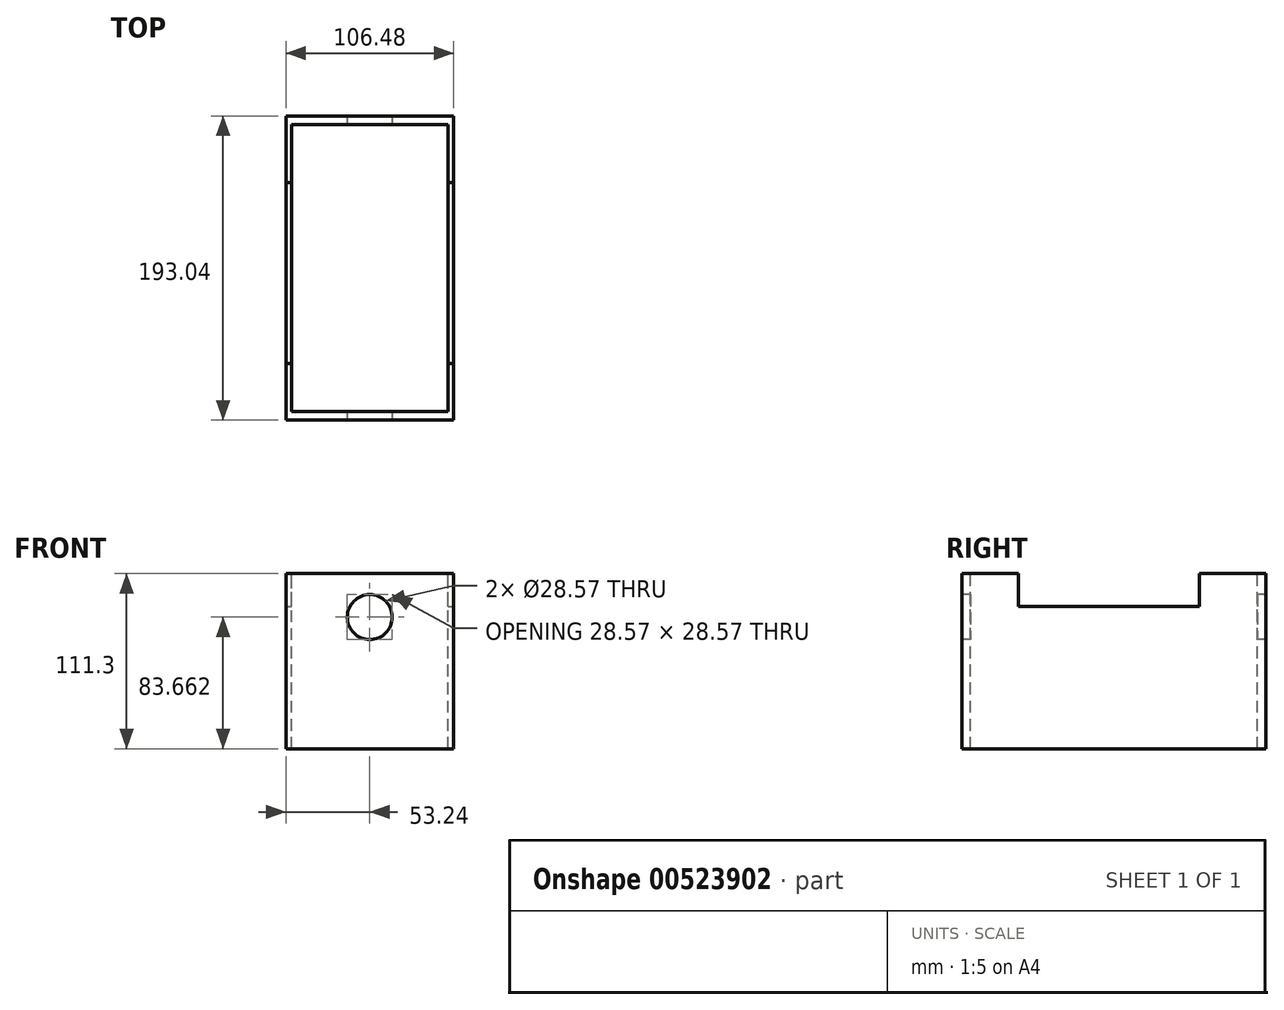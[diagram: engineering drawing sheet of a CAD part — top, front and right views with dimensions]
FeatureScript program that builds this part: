
annotation { "Feature Type Name" : "Feature", "Feature Type Description" : "" }
export const myFeature = defineFeature(function(context is Context, id is Id, definition is map)
    precondition{}
    {
        {
            var Q0;
            Q0=qCreatedBy(makeId("Front.planeOp"),FACE);
            var sketch = newSketch(context, id + "F0", { "sketchPlane" : qUnion([Q0])});
            skLineSegment(sketch, "E0.bottom", {"start": v(53.24, -55.65) * mm, "end": v(-53.24, -55.65) * mm});
            skLineSegment(sketch, "E0.top", {"start": v(53.24, 55.65) * mm, "end": v(-53.24, 55.65) * mm});
            skLineSegment(sketch, "E0.left", {"start": v(53.24, -55.65) * mm, "end": v(53.24, 55.65) * mm});
            skLineSegment(sketch, "E0.right", {"start": v(-53.24, -55.65) * mm, "end": v(-53.24, 55.65) * mm});
            skPoint(sketch, "E0.middle", {"position": v(0, 0) * mm});
            skSolve(sketch);
        }
        {
            var Q0;
            Q0=makeQuery(id+"F0.imprint","IMPRINT",FACE,{"disambiguationData":[TD([[makeQuery(id+"F0.imprint","IMPRINT",EDGE,{"derivedFrom":sQuery(id+"F0.wireOp",EDGE,"E0.bottom")}),-1.0]])]});
            extrude(context, id + "F1", {"entities" : qUnion([Q0]), "endBound" : BoundingType.SYMMETRIC, "depth" : 193.04 * mm, "offsetDistance" : 25.4 * mm});
        }
        {
            var Q0;
            Q0=makeQuery(id+"F1.opExtrude","SWEPT_FACE",FACE,{"disambiguationData":[OSD([sQuery(id+"F0.wireOp",EDGE,"E0.top")])]});
            var sketch = newSketch(context, id + "F2", { "sketchPlane" : qUnion([Q0])});
            skLineSegment(sketch, "E1.bottom", {"start": v(49.77, 91.2) * mm, "end": v(-49.77, 91.2) * mm});
            skLineSegment(sketch, "E1.top", {"start": v(49.77, -91.2) * mm, "end": v(-49.77, -91.2) * mm});
            skLineSegment(sketch, "E1.left", {"start": v(49.77, 91.2) * mm, "end": v(49.77, -91.2) * mm});
            skLineSegment(sketch, "E1.right", {"start": v(-49.77, 91.2) * mm, "end": v(-49.77, -91.2) * mm});
            skPoint(sketch, "E1.middle", {"position": v(0, 0) * mm});
            skSolve(sketch);
        }
        {
            var Q0;
            Q0=makeQuery(id+"F2.imprint","IMPRINT",FACE,{"disambiguationData":[TD([[makeQuery(id+"F2.imprint","IMPRINT",EDGE,{"derivedFrom":sQuery(id+"F2.wireOp",EDGE,"E1.bottom")}),1.0]])]});
            extrude(context, id + "F3", {"entities" : qUnion([Q0]), "operationType" : NewBodyOperationType.REMOVE, "oppositeDirection" : true, "depth" : 181.36 * mm, "offsetDistance" : 25.4 * mm});
        }
        {
            var Q0;
            Q0=makeQuery(id+"F1.opExtrude","SWEPT_FACE",FACE,{"disambiguationData":[OSD([sQuery(id+"F0.wireOp",EDGE,"E0.left")])]});
            var sketch = newSketch(context, id + "F4", { "sketchPlane" : qUnion([Q0])});
            skLineSegment(sketch, "E2.bottom", {"start": v(-60.67, 55.65) * mm, "end": v(54.28, 55.65) * mm});
            skLineSegment(sketch, "E2.top", {"start": v(-60.67, 34.72) * mm, "end": v(54.28, 34.72) * mm});
            skLineSegment(sketch, "E2.left", {"start": v(-60.67, 55.65) * mm, "end": v(-60.67, 34.72) * mm});
            skLineSegment(sketch, "E2.right", {"start": v(54.28, 55.65) * mm, "end": v(54.28, 34.72) * mm});
            skSolve(sketch);
        }
        {
            var Q0;
            Q0=makeQuery(id+"F4.imprint","IMPRINT",FACE,{"disambiguationData":[TD([[makeQuery(id+"F4.imprint","IMPRINT",EDGE,{"derivedFrom":sQuery(id+"F4.wireOp",EDGE,"E2.bottom")}),-1.0]])]});
            extrude(context, id + "F5", {"entities" : qUnion([Q0]), "operationType" : NewBodyOperationType.REMOVE, "oppositeDirection" : true, "depth" : 135.13 * mm, "offsetDistance" : 25.4 * mm});
        }
        {
            var Q0;
            Q0=makeQuery(id+"F1.opExtrude","CAP_FACE",FACE,{"disambiguationData":[OSD([sQuery(id+"F0.wireOp",EDGE,"E0.bottom"),sQuery(id+"F0.wireOp",EDGE,"E0.top"),sQuery(id+"F0.wireOp",EDGE,"E0.left"),sQuery(id+"F0.wireOp",EDGE,"E0.right")])],"isStart":false});
            var sketch = newSketch(context, id + "F6", { "sketchPlane" : qUnion([Q0])});
            skCircle(sketch, "E3", {"center": v(0, 28.01) * mm, "radius": 14.28 * mm});
            skSolve(sketch);
        }
        {
            var Q0;
            Q0=makeQuery(id+"F6.imprint","IMPRINT",FACE,{"disambiguationData":[TD([[makeQuery(id+"F6.imprint","IMPRINT",EDGE,{"derivedFrom":sQuery(id+"F6.wireOp",EDGE,"E3")}),1.0]])]});
            extrude(context, id + "F7", {"entities" : qUnion([Q0]), "operationType" : NewBodyOperationType.REMOVE, "oppositeDirection" : true, "depth" : 257.3 * mm, "offsetDistance" : 25.4 * mm});
        }
    });
